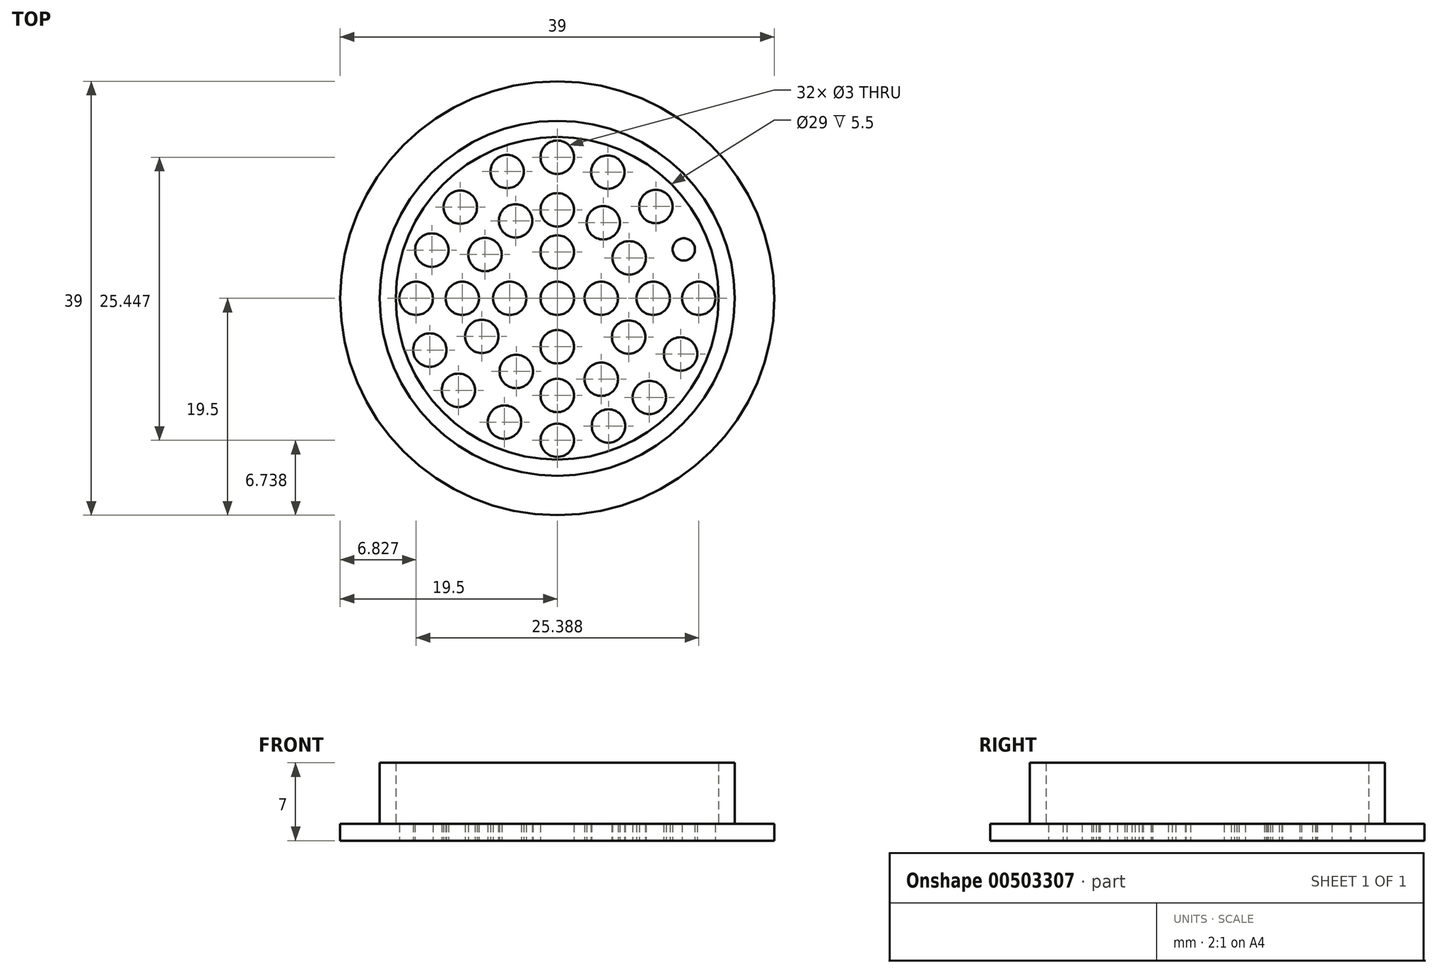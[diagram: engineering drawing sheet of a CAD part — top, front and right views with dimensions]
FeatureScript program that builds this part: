
annotation { "Feature Type Name" : "Feature", "Feature Type Description" : "" }
export const myFeature = defineFeature(function(context is Context, id is Id, definition is map)
    precondition{}
    {
        {
            var Q0;
            Q0=qCreatedBy(makeId("Top.planeOp"),FACE);
            var sketch = newSketch(context, id + "F0", { "sketchPlane" : qUnion([Q0])});
            skCircle(sketch, "E0", {"center": v(0, 0) * mm, "radius": 19.5 * mm});
            skSolve(sketch);
        }
        {
            var Q0;
            Q0 = qSketchRegion(id + "F0", true);
            extrude(context, id + "F1", {"entities" : qUnion([Q0]), "depth" : 1.5 * mm});
        }
        {
            var Q0;
            Q0=qCreatedBy(makeId("Top.planeOp"),FACE);
            var sketch = newSketch(context, id + "F2", { "sketchPlane" : qUnion([Q0])});
            skCircle(sketch, "E1", {"center": v(0, 0) * mm, "radius": 15.95 * mm});
            skCircle(sketch, "E2", {"center": v(0, 0) * mm, "radius": 14.5 * mm});
            skSolve(sketch);
        }
        {
            var Q0;
            Q0 = qSketchRegion(id + "F2", true);
            extrude(context, id + "F3", {"entities" : qUnion([Q0]), "operationType" : NewBodyOperationType.ADD, "depth" : 7 * mm});
        }
        {
            var Q0;
            Q0=qCreatedBy(makeId("Top.planeOp"),FACE);
            var sketch = newSketch(context, id + "F4", { "sketchPlane" : qUnion([Q0])});
            skCircle(sketch, "E3", {"center": v(0, 0) * mm, "radius": 1.5 * mm});
            skCircle(sketch, "E4", {"center": v(0, 4.16) * mm, "radius": 1.5 * mm});
            skCircle(sketch, "E5", {"center": v(0, -4.36) * mm, "radius": 1.5 * mm});
            skCircle(sketch, "E6", {"center": v(0, -8.74) * mm, "radius": 1.5 * mm});
            skCircle(sketch, "E7", {"center": v(0, -12.76) * mm, "radius": 1.5 * mm});
            skCircle(sketch, "E8", {"center": v(0, 7.96) * mm, "radius": 1.5 * mm});
            skCircle(sketch, "E9", {"center": v(0, 12.68) * mm, "radius": 1.5 * mm});
            skCircle(sketch, "E10", {"center": v(-4.27, 0) * mm, "radius": 1.5 * mm});
            skCircle(sketch, "E11", {"center": v(-8.53, 0) * mm, "radius": 1.5 * mm});
            skCircle(sketch, "E12", {"center": v(-12.67, 0) * mm, "radius": 1.5 * mm});
            skCircle(sketch, "E13", {"center": v(3.96, 0) * mm, "radius": 1.5 * mm});
            skCircle(sketch, "E14", {"center": v(8.63, 0) * mm, "radius": 1.5 * mm});
            skCircle(sketch, "E15", {"center": v(12.72, 0) * mm, "radius": 1.5 * mm});
            skCircle(sketch, "E16", {"center": v(-6.49, 3.93) * mm, "radius": 1.5 * mm});
            skCircle(sketch, "E17", {"center": v(-11.27, 4.34) * mm, "radius": 1.5 * mm});
            skCircle(sketch, "E18", {"center": v(-8.7, 8.2) * mm, "radius": 1.5 * mm});
            skCircle(sketch, "E19", {"center": v(-4.5, 11.4) * mm, "radius": 1.5 * mm});
            skCircle(sketch, "E20", {"center": v(4.54, 11.34) * mm, "radius": 1.5 * mm});
            skCircle(sketch, "E21", {"center": v(8.86, 8.25) * mm, "radius": 1.5 * mm});
            skCircle(sketch, "E22", {"center": v(11.37, 4.4) * mm, "radius": 1 * mm});
            skCircle(sketch, "E23", {"center": v(11.08, -5) * mm, "radius": 1.5 * mm});
            skCircle(sketch, "E24", {"center": v(8.28, -8.91) * mm, "radius": 1.5 * mm});
            skCircle(sketch, "E25", {"center": v(4.6, -11.48) * mm, "radius": 1.5 * mm});
            skCircle(sketch, "E26", {"center": v(-4.74, -11.13) * mm, "radius": 1.5 * mm});
            skCircle(sketch, "E27", {"center": v(-8.88, -8.27) * mm, "radius": 1.5 * mm});
            skCircle(sketch, "E28", {"center": v(-11.45, -4.65) * mm, "radius": 1.5 * mm});
            skCircle(sketch, "E29", {"center": v(-6.78, -3.42) * mm, "radius": 1.5 * mm});
            skCircle(sketch, "E30", {"center": v(-3.69, -6.58) * mm, "radius": 1.5 * mm});
            skCircle(sketch, "E31", {"center": v(3.96, -7.28) * mm, "radius": 1.5 * mm});
            skCircle(sketch, "E32", {"center": v(6.41, -3.48) * mm, "radius": 1.5 * mm});
            skCircle(sketch, "E33", {"center": v(6.47, 3.64) * mm, "radius": 1.5 * mm});
            skCircle(sketch, "E34", {"center": v(4.14, 6.79) * mm, "radius": 1.5 * mm});
            skCircle(sketch, "E35", {"center": v(-3.74, 6.96) * mm, "radius": 1.5 * mm});
            skSolve(sketch);
        }
        {
            var Q0;
            Q0 = qSketchRegion(id + "F4", true);
            extrude(context, id + "F5", {"entities" : qUnion([Q0]), "operationType" : NewBodyOperationType.REMOVE, "depth" : 25 * mm});
        }
    });
